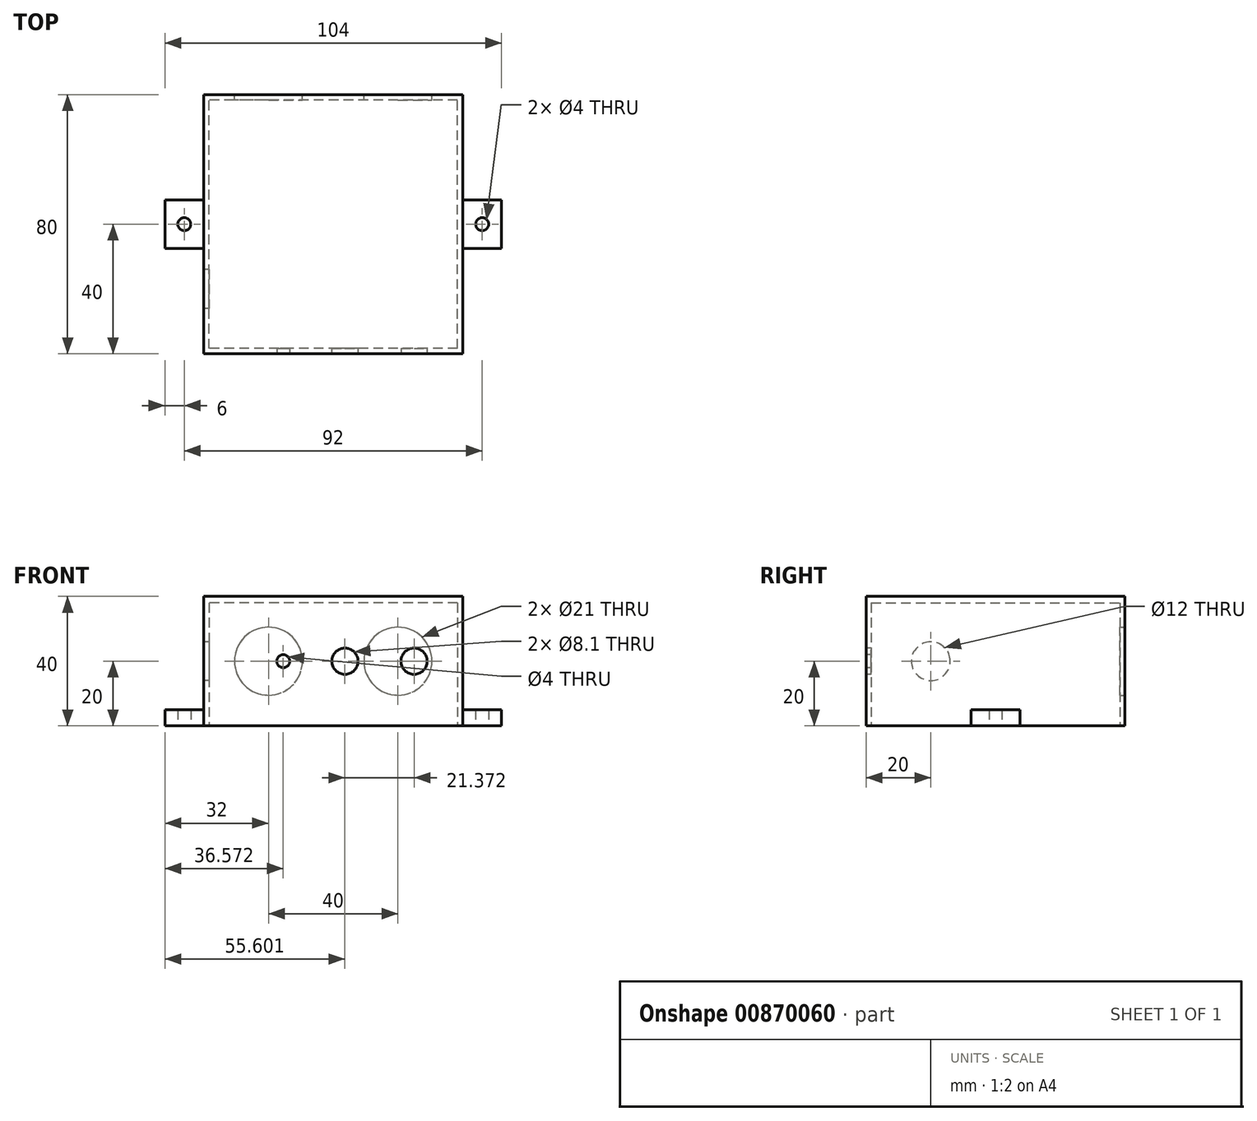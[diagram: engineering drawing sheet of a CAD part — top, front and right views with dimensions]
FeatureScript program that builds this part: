
annotation { "Feature Type Name" : "Feature", "Feature Type Description" : "" }
export const myFeature = defineFeature(function(context is Context, id is Id, definition is map)
    precondition{}
    {
        {
            var Q0;
            Q0=qCreatedBy(makeId("Top.planeOp"),FACE);
            var sketch = newSketch(context, id + "F0", { "sketchPlane" : qUnion([Q0])});
            skLineSegment(sketch, "E0.bottom", {"start": v(40, -40) * mm, "end": v(-40, -40) * mm});
            skLineSegment(sketch, "E0.top", {"start": v(40, 40) * mm, "end": v(-40, 40) * mm});
            skLineSegment(sketch, "E0.left", {"start": v(40, -40) * mm, "end": v(40, 40) * mm});
            skLineSegment(sketch, "E0.right", {"start": v(-40, -40) * mm, "end": v(-40, 40) * mm});
            skPoint(sketch, "E0.middle", {"position": v(0, 0) * mm});
            skLineSegment(sketch, "E1.0", {"start": v(-38.4, -38.4) * mm, "end": v(-38.4, 38.4) * mm});
            skLineSegment(sketch, "E1.1", {"start": v(38.4, -38.4) * mm, "end": v(-38.4, -38.4) * mm});
            skLineSegment(sketch, "E2.0", {"start": v(38.4, 38.4) * mm, "end": v(-38.4, 38.4) * mm});
            skLineSegment(sketch, "E2.1", {"start": v(38.4, -38.4) * mm, "end": v(38.4, 38.4) * mm});
            skLineSegment(sketch, "E3.bottom", {"start": v(-52, 7.5) * mm, "end": v(-40, 7.5) * mm});
            skLineSegment(sketch, "E3.top", {"start": v(-52, -7.5) * mm, "end": v(-40, -7.5) * mm});
            skLineSegment(sketch, "E3.left", {"start": v(-52, 7.5) * mm, "end": v(-52, -7.5) * mm});
            skPoint(sketch, "E3.middle", {"position": v(-40, 0) * mm});
            skPoint(sketch, "E3.right.start.orphan", {"position": v(-28, 7.5) * mm});
            skPoint(sketch, "E4.orphan", {"position": v(-28, -7.5) * mm});
            skLineSegment(sketch, "E5.bottom", {"start": v(52, -7.5) * mm, "end": v(40, -7.5) * mm});
            skLineSegment(sketch, "E5.top", {"start": v(52, 7.5) * mm, "end": v(40, 7.5) * mm});
            skLineSegment(sketch, "E5.left", {"start": v(52, -7.5) * mm, "end": v(52, 7.5) * mm});
            skPoint(sketch, "E5.middle", {"position": v(40, 0) * mm});
            skPoint(sketch, "E6.trimOffspring.end.orphan", {"position": v(28, 7.5) * mm});
            skPoint(sketch, "E7.orphan", {"position": v(28, -7.5) * mm});
            skCircle(sketch, "E8", {"center": v(-46, 0) * mm, "radius": 2 * mm});
            skCircle(sketch, "E9", {"center": v(46, 0) * mm, "radius": 2 * mm});
            skSolve(sketch);
        }
        {
            var Q0;
            {var subQ1=sQuery(id+"F0.wireOp",EDGE,"E3.bottom");Q0=makeQuery(id+"F0.imprint","IMPRINT",FACE,{"disambiguationData":[TD([[makeQuery(id+"F0.imprint","IMPRINT",EDGE,{"derivedFrom":subQ1}),-1.0]])]});}
            var Q1;
            {var subQ1=sQuery(id+"F0.wireOp",EDGE,"E5.bottom");Q1=makeQuery(id+"F0.imprint","IMPRINT",FACE,{"disambiguationData":[TD([[makeQuery(id+"F0.imprint","IMPRINT",EDGE,{"derivedFrom":subQ1}),-1.0]])]});}
            extrude(context, id + "F1", {"entities" : qUnion([Q0, Q1]), "depth" : 5 * mm, "offsetDistance" : 25 * mm});
        }
        {
            var Q0;
            {var subQ4=sQuery(id+"F0.wireOp",EDGE,"E0.bottom");Q0=makeQuery(id+"F0.imprint","IMPRINT",FACE,{"disambiguationData":[TD([[makeQuery(id+"F0.imprint","IMPRINT",EDGE,{"derivedFrom":subQ4}),-1.0]])]});}
            extrude(context, id + "F2", {"entities" : qUnion([Q0]), "depth" : 40 * mm, "offsetDistance" : 25 * mm});
        }
        {
            var Q0;
            Q0=makeQuery(id+"F2.opExtrude","CAP_FACE",FACE,{"disambiguationData":[OSD([sQuery(id+"F0.wireOp",EDGE,"E0.bottom"),sQuery(id+"F0.wireOp",EDGE,"E0.top"),sQuery(id+"F0.wireOp",EDGE,"E0.left"),sQuery(id+"F0.wireOp",EDGE,"E0.right"),sQuery(id+"F0.wireOp",EDGE,"E1.0"),sQuery(id+"F0.wireOp",EDGE,"E1.1"),sQuery(id+"F0.wireOp",EDGE,"E2.0"),sQuery(id+"F0.wireOp",EDGE,"E2.1")])],"isStart":false});
            var sketch = newSketch(context, id + "F3", { "sketchPlane" : qUnion([Q0])});
            skSolve(sketch);
        }
        {
            var Q0;
            Q0=makeQuery(id+"F3.imprint","IMPRINT",FACE,{"disambiguationData":[TD([[makeQuery(id+"F3.imprint","IMPRINT",EDGE,{"derivedFrom":makeQuery(id+"F2.opExtrude","CAP_EDGE",EDGE,{"disambiguationData":[OSD([sQuery(id+"F0.wireOp",EDGE,"E1.0")])],"isStart":false})}),-1.0]])]});
            extrude(context, id + "F4", {"entities" : qUnion([Q0]), "operationType" : NewBodyOperationType.ADD, "oppositeDirection" : true, "depth" : 2 * mm, "offsetDistance" : 25 * mm});
        }
        {
            var Q0;
            Q0=makeQuery(id+"F2.opExtrude","SWEPT_FACE",FACE,{"disambiguationData":[OSD([sQuery(id+"F0.wireOp",EDGE,"E0.top")])]});
            var sketch = newSketch(context, id + "F5", { "sketchPlane" : qUnion([Q0])});
            skCircle(sketch, "E10", {"center": v(20, 20) * mm, "radius": 10.5 * mm});
            skCircle(sketch, "E11", {"center": v(-20, 20) * mm, "radius": 10.5 * mm});
            skPoint(sketch, "E12.end.orphan", {"position": v(-40, 0) * mm});
            skPoint(sketch, "E13.orphan", {"position": v(0, 40) * mm});
            skPoint(sketch, "E14.start.orphan", {"position": v(40, 0) * mm});
            skSolve(sketch);
        }
        {
            var Q0;
            Q0=makeQuery(id+"F5.imprint","IMPRINT",FACE,{"disambiguationData":[TD([[makeQuery(id+"F5.imprint","IMPRINT",EDGE,{"derivedFrom":sQuery(id+"F5.wireOp",EDGE,"E11")}),1.0]])]});
            var Q1;
            Q1=makeQuery(id+"F5.imprint","IMPRINT",FACE,{"disambiguationData":[TD([[makeQuery(id+"F5.imprint","IMPRINT",EDGE,{"derivedFrom":sQuery(id+"F5.wireOp",EDGE,"E10")}),1.0]])]});
            extrude(context, id + "F6", {"entities" : qUnion([Q0, Q1]), "operationType" : NewBodyOperationType.REMOVE, "oppositeDirection" : true, "depth" : 25 * mm, "offsetDistance" : 25 * mm});
        }
        {
            var Q0;
            Q0=makeQuery(id+"F2.opExtrude","SWEPT_FACE",FACE,{"disambiguationData":[OSD([sQuery(id+"F0.wireOp",EDGE,"E0.right")])]});
            var sketch = newSketch(context, id + "F7", { "sketchPlane" : qUnion([Q0])});
            skCircle(sketch, "E15", {"center": v(20, 20) * mm, "radius": 6 * mm});
            skPoint(sketch, "E16.orphan", {"position": v(40, 0) * mm});
            skPoint(sketch, "E17.start.orphan", {"position": v(0, 40) * mm});
            skSolve(sketch);
        }
        {
            var Q0;
            Q0=makeQuery(id+"F7.imprint","IMPRINT",FACE,{"disambiguationData":[TD([[makeQuery(id+"F7.imprint","IMPRINT",EDGE,{"derivedFrom":sQuery(id+"F7.wireOp",EDGE,"E15")}),1.0]])]});
            extrude(context, id + "F8", {"entities" : qUnion([Q0]), "operationType" : NewBodyOperationType.REMOVE, "oppositeDirection" : true, "depth" : 25 * mm, "offsetDistance" : 25 * mm});
        }
        {
            var Q0;
            Q0=makeQuery(id+"F2.opExtrude","SWEPT_FACE",FACE,{"disambiguationData":[OSD([sQuery(id+"F0.wireOp",EDGE,"E0.bottom")])]});
            var sketch = newSketch(context, id + "F9", { "sketchPlane" : qUnion([Q0])});
            skCircle(sketch, "E18", {"center": v(24.97, 20) * mm, "radius": 4.05 * mm});
            skCircle(sketch, "E19", {"center": v(3.6, 20) * mm, "radius": 4.05 * mm});
            skCircle(sketch, "E20", {"center": v(-15.43, 20) * mm, "radius": 2 * mm});
            skPoint(sketch, "E21.orphan", {"position": v(40, 20) * mm});
            skPoint(sketch, "E22.orphan", {"position": v(-40, 20) * mm});
            skSolve(sketch);
        }
        {
            var Q0;
            Q0=makeQuery(id+"F9.imprint","IMPRINT",FACE,{"disambiguationData":[TD([[makeQuery(id+"F9.imprint","IMPRINT",EDGE,{"derivedFrom":sQuery(id+"F9.wireOp",EDGE,"E18")}),1.0]])]});
            var Q1;
            Q1=makeQuery(id+"F9.imprint","IMPRINT",FACE,{"disambiguationData":[TD([[makeQuery(id+"F9.imprint","IMPRINT",EDGE,{"derivedFrom":sQuery(id+"F9.wireOp",EDGE,"E19")}),1.0]])]});
            var Q2;
            Q2=makeQuery(id+"F9.imprint","IMPRINT",FACE,{"disambiguationData":[TD([[makeQuery(id+"F9.imprint","IMPRINT",EDGE,{"derivedFrom":sQuery(id+"F9.wireOp",EDGE,"E20")}),1.0]])]});
            extrude(context, id + "F10", {"entities" : qUnion([Q0, Q1, Q2]), "operationType" : NewBodyOperationType.REMOVE, "oppositeDirection" : true, "depth" : 25 * mm, "offsetDistance" : 25 * mm});
        }
    });
